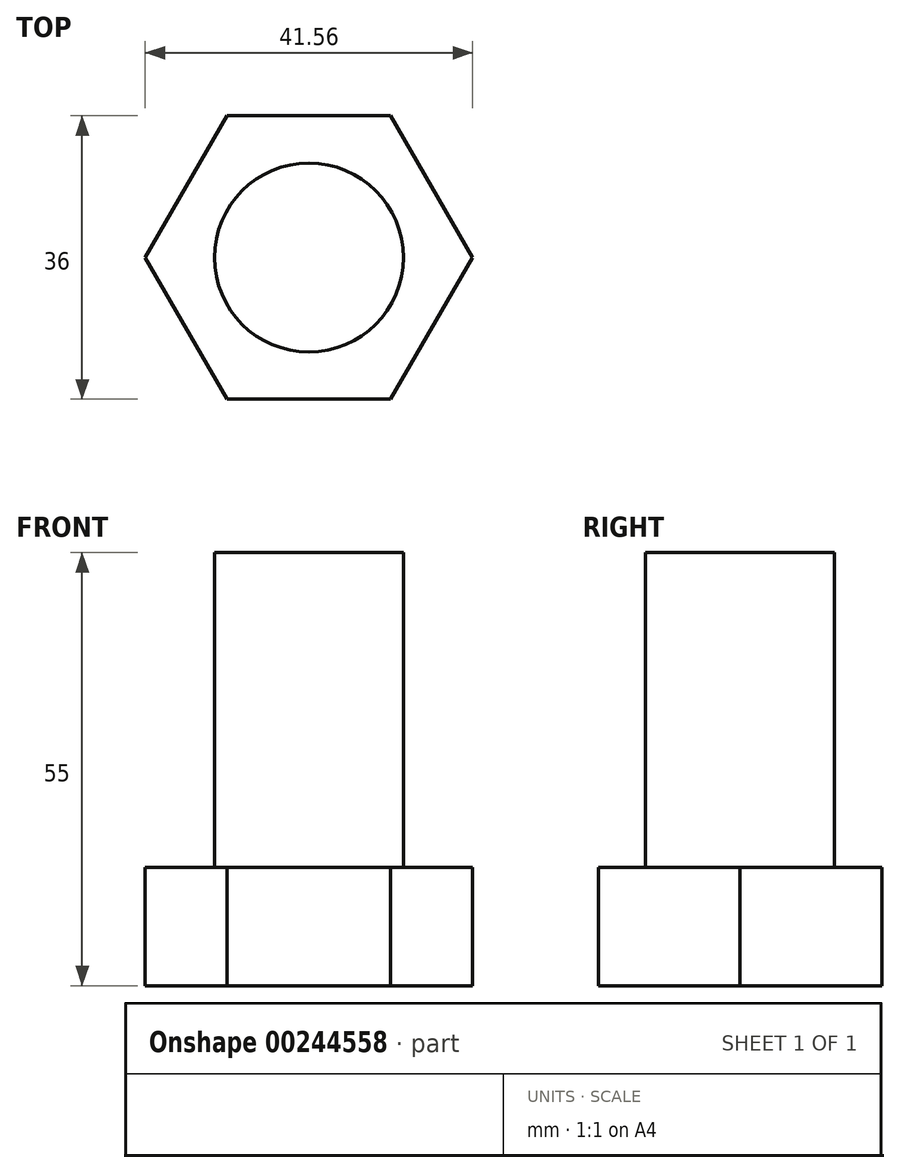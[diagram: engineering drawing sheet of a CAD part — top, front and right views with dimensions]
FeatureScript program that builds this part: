
annotation { "Feature Type Name" : "Feature", "Feature Type Description" : "" }
export const myFeature = defineFeature(function(context is Context, id is Id, definition is map)
    precondition{}
    {
        {
            var Q0;
            Q0=qCreatedBy(makeId("Top.planeOp"),FACE);
            var sketch = newSketch(context, id + "F0", { "sketchPlane" : qUnion([Q0])});
            skCircle(sketch, "E0", {"center": v(0, 0) * mm, "radius": 12 * mm});
            skSolve(sketch);
        }
        {
            var Q0;
            Q0=makeQuery(id+"F0.imprint","IMPRINT",FACE,{"disambiguationData":[TD([[makeQuery(id+"F0.imprint","IMPRINT",EDGE,{"derivedFrom":sQuery(id+"F0.wireOp",EDGE,"E0")}),1.0]])]});
            extrude(context, id + "F1", {"entities" : qUnion([Q0]), "depth" : 40 * mm});
        }
        {
            var Q0;
            Q0=qCreatedBy(makeId("Top.planeOp"),FACE);
            var sketch = newSketch(context, id + "F2", { "sketchPlane" : qUnion([Q0])});
            skCircle(sketch, "E1.cCircle", {"center": v(0, 0) * mm, "radius": 18 * mm, "construction": true});
            skLineSegment(sketch, "E1.0", {"start": v(10.4, 18) * mm, "end": v(20.78, 0) * mm});
            skLineSegment(sketch, "E1.1", {"start": v(20.78, 0) * mm, "end": v(10.4, -18) * mm});
            skLineSegment(sketch, "E1.2", {"start": v(10.4, -18) * mm, "end": v(-10.4, -18) * mm});
            skLineSegment(sketch, "E1.3", {"start": v(-10.4, -18) * mm, "end": v(-20.78, 0) * mm});
            skLineSegment(sketch, "E1.4", {"start": v(-20.78, 0) * mm, "end": v(-10.4, 18) * mm});
            skLineSegment(sketch, "E1.5", {"start": v(-10.4, 18) * mm, "end": v(10.4, 18) * mm});
            skPoint(sketch, "E1.0.midPoint", {"position": v(15.59, 9) * mm});
            skSolve(sketch);
        }
        {
            var Q0;
            Q0=makeQuery(id+"F2.imprint","IMPRINT",FACE,{"disambiguationData":[TD([[makeQuery(id+"F2.imprint","IMPRINT",EDGE,{"derivedFrom":sQuery(id+"F2.wireOp",EDGE,"E1.0")}),-1.0]])]});
            extrude(context, id + "F3", {"entities" : qUnion([Q0]), "operationType" : NewBodyOperationType.ADD, "oppositeDirection" : true, "depth" : 15 * mm});
        }
    });
